# Revit family: Indoor_Pendant Lamp_Santa&Cole_Sistema Fonda
name_source: partatom
category: Luminarias
revit_build: Autodesk Revit 2018 (Build: 20190510_1515(x64)
units: mm (PartAtom-declared; Revit-internal decimal feet)

## family parameters
Compartido = No
Corte con vacíos al cargar = No
Cota de conector redondo = Diámetro de uso
Origen de luz = No
Punto de cálculo de habitación = No
Tipo de pieza = Normal

## types (1)
- Indoor_Pendant Lamp_Santa&Cole_Sistema Fonda
    Assembly Instructions - CE = https://www.santacole.com
    Assembly Instructions - UL = https://www.santacole.com
    Code = FONxx+Pxx0x+FONxx+CSF01+FSC13
    EC = Part Type : End Cap
    Energy Label = https://www.santacole.com
    Fabricante = Santa & Cole
    J = Part Type : Join
    LC = Part Type : Left Corner
    Manufacturer website = https://www.santacole.com
    Modelo = Sistema Fonda
    RC = Part Type : Right Corner
    Technical Information = https://www.santacole.com
    URL = https://www.santacole.com
    VC = Part Type : Void Corner
    VP = Part Type : Void Cap
    Voltaje (100-230 V) = 120 V
